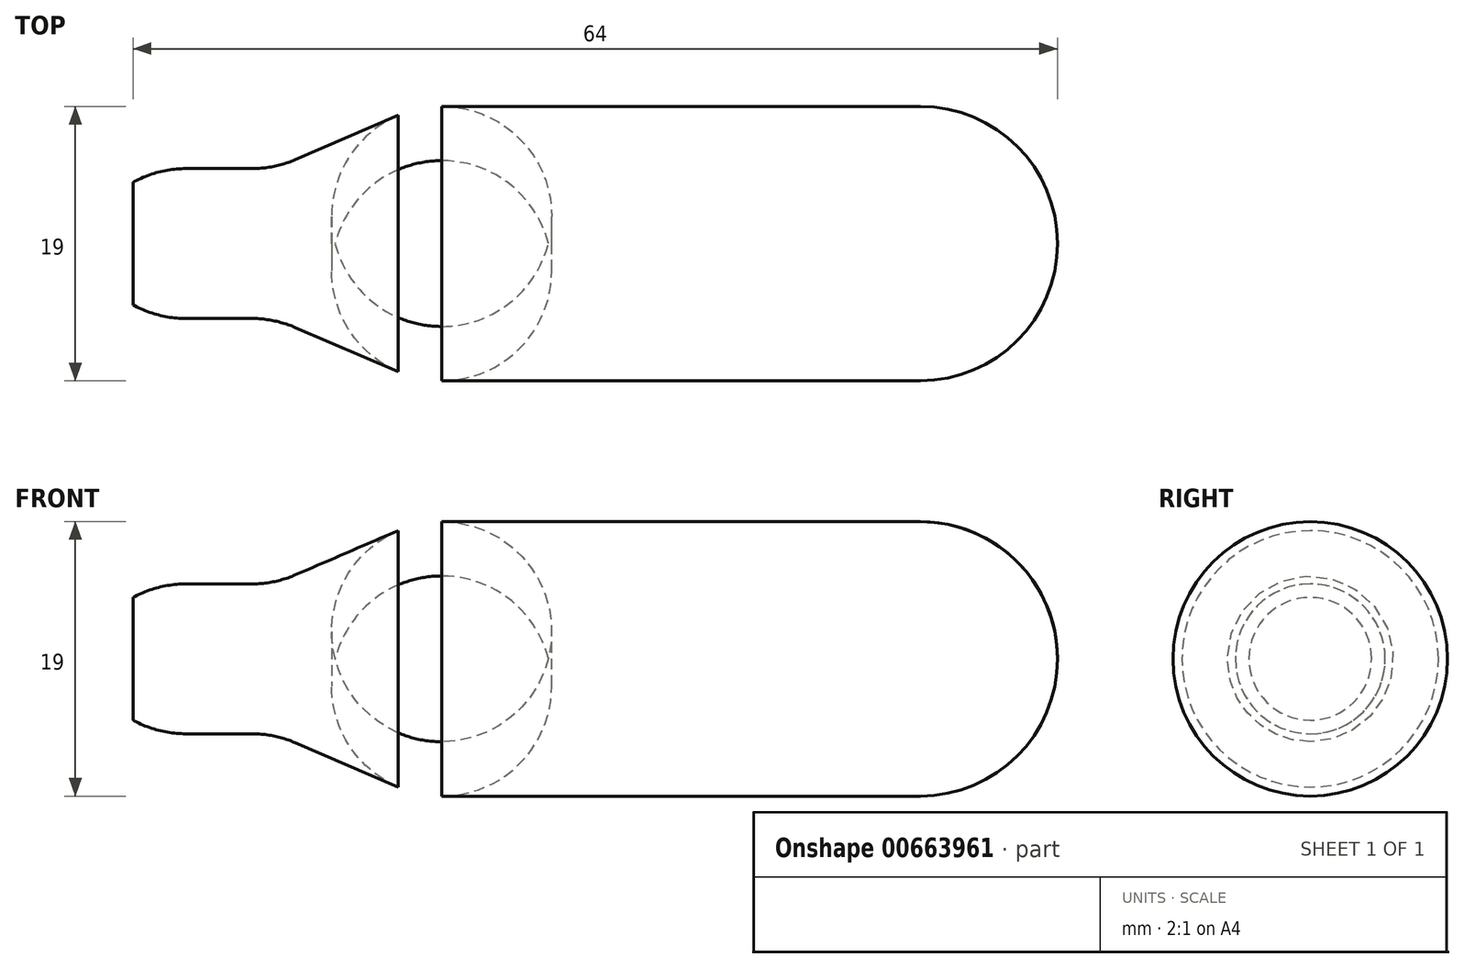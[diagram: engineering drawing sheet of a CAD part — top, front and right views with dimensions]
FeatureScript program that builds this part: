
annotation { "Feature Type Name" : "Feature", "Feature Type Description" : "" }
export const myFeature = defineFeature(function(context is Context, id is Id, definition is map)
    precondition{}
    {
        {
            var Q0;
            Q0=qCreatedBy(makeId("Front.planeOp"),FACE);
            var sketch = newSketch(context, id + "F0", { "sketchPlane" : qUnion([Q0])});
            skLineSegment(sketch, "E0", {"start": v(0, 0) * mm, "end": v(0, 4.25) * mm});
            skLineSegment(sketch, "E1", {"start": v(0, 0) * mm, "end": v(64, 0) * mm});
            skLineSegment(sketch, "E2", {"start": v(0, 4.25) * mm, "end": v(1.77, 5.19) * mm});
            skLineSegment(sketch, "E3", {"start": v(1.77, 5.19) * mm, "end": v(9.77, 5.19) * mm});
            skLineSegment(sketch, "E4", {"start": v(64, 9.5) * mm, "end": v(19.8, 9.5) * mm});
            skLineSegment(sketch, "E5", {"start": v(19.8, 9.5) * mm, "end": v(9.77, 5.19) * mm});
            skLineSegment(sketch, "E6", {"start": v(64, 0) * mm, "end": v(64, 9.5) * mm});
            skSolve(sketch);
        }
        {
            var Q0;
            Q0 = qSketchRegion(id + "F0", true);
            var Q1;
            Q1=sQuery(id+"F0.wireOp",EDGE,"E1");
            revolve(context, id + "F1", {"entities" : qUnion([Q0]), "axis" : qUnion([Q1]), "revolveType" : RevolveType.FULL});
        }
        {
            var Q0;
            Q0=makeQuery(id+"F1.opRevolve","SWEPT_EDGE",EDGE,{"disambiguationData":[OSD([sQuery(id+"F0.wireOp",EDGE,"E4"),sQuery(id+"F0.wireOp",EDGE,"E6")])]});
            fillet(context, id + "F2", {"entities" : qUnion([Q0]), "radius" : 9.5 * mm, "tangentPropagation" : true, "allowEdgeOverflow" : false});
        }
        {
            var Q0;
            Q0=makeQuery(id+"F1.opRevolve","SWEPT_EDGE",EDGE,{"disambiguationData":[OSD([sQuery(id+"F0.wireOp",EDGE,"E4"),sQuery(id+"F0.wireOp",EDGE,"E5")])]});
            var Q1;
            Q1=makeQuery(id+"F1.opRevolve","SWEPT_EDGE",EDGE,{"disambiguationData":[OSD([sQuery(id+"F0.wireOp",EDGE,"E2"),sQuery(id+"F0.wireOp",EDGE,"E3")])]});
            var Q2;
            Q2=makeQuery(id+"F1.opRevolve","SWEPT_EDGE",EDGE,{"disambiguationData":[OSD([sQuery(id+"F0.wireOp",EDGE,"E3"),sQuery(id+"F0.wireOp",EDGE,"E5")])]});
            fillet(context, id + "F3", {"entities" : qUnion([Q0, Q1, Q2]), "radius" : 7.62 * mm, "tangentPropagation" : true, "allowEdgeOverflow" : false});
        }
    });
